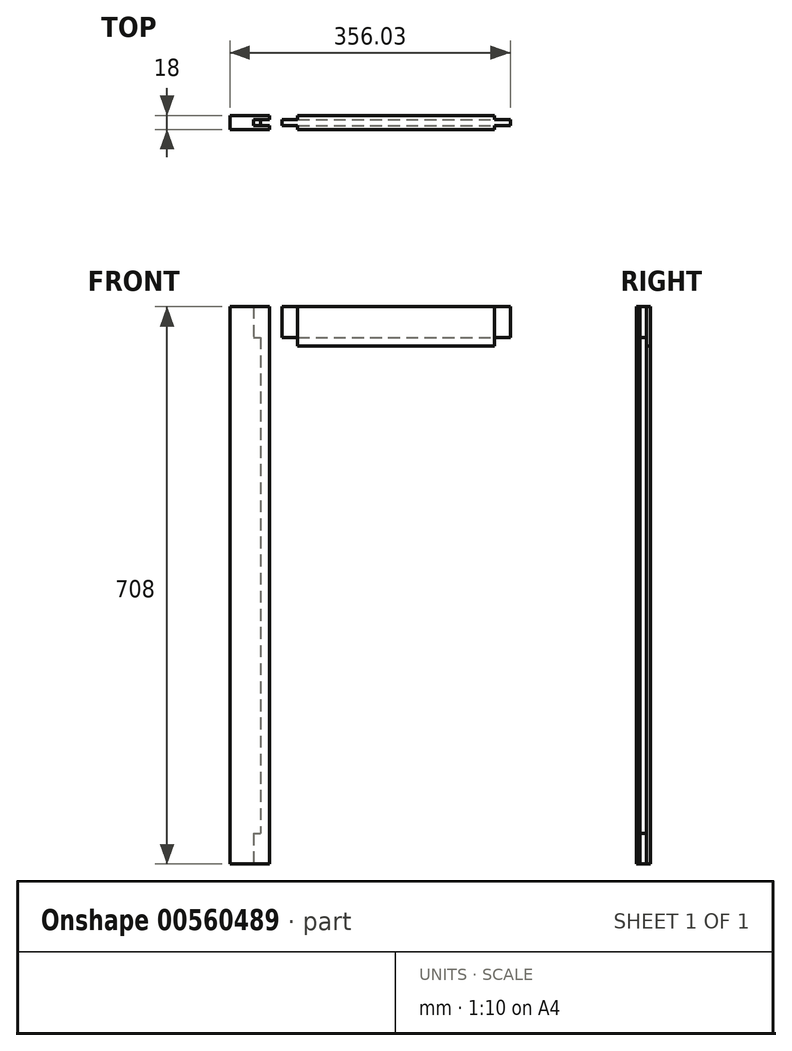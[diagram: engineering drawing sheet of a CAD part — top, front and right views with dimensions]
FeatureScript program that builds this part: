
annotation { "Feature Type Name" : "Feature", "Feature Type Description" : "" }
export const myFeature = defineFeature(function(context is Context, id is Id, definition is map)
    precondition{}
    {
        {
            var Q0;
            Q0=qCreatedBy(makeId("Front.planeOp"),FACE);
            var sketch = newSketch(context, id + "F0", { "sketchPlane" : qUnion([Q0])});
            skLineSegment(sketch, "E0.bottom", {"start": v(-16.71, 354) * mm, "end": v(-66.71, 354) * mm});
            skLineSegment(sketch, "E0.top", {"start": v(-16.71, -354) * mm, "end": v(-66.71, -354) * mm});
            skLineSegment(sketch, "E0.left", {"start": v(-16.71, 354) * mm, "end": v(-16.71, -354) * mm});
            skLineSegment(sketch, "E0.right", {"start": v(-66.71, 354) * mm, "end": v(-66.71, -354) * mm});
            skPoint(sketch, "E0.middle", {"position": v(-41.71, 0) * mm});
            skLineSegment(sketch, "E1.bottom", {"start": v(344.89, 354) * mm, "end": v(294.89, 354) * mm});
            skLineSegment(sketch, "E1.top", {"start": v(344.89, -354) * mm, "end": v(294.89, -354) * mm});
            skLineSegment(sketch, "E1.left", {"start": v(344.89, 354) * mm, "end": v(344.89, -354) * mm});
            skLineSegment(sketch, "E1.right", {"start": v(294.89, 354) * mm, "end": v(294.89, -354) * mm});
            skPoint(sketch, "E1.middle", {"position": v(319.89, 0) * mm});
            skLineSegment(sketch, "E2.bottom", {"start": v(19.32, 354) * mm, "end": v(269.32, 354) * mm});
            skLineSegment(sketch, "E2.top", {"start": v(19.32, 304) * mm, "end": v(269.32, 304) * mm});
            skLineSegment(sketch, "E2.left", {"start": v(19.32, 354) * mm, "end": v(19.32, 304) * mm});
            skLineSegment(sketch, "E2.right", {"start": v(269.32, 354) * mm, "end": v(269.32, 304) * mm});
            skLineSegment(sketch, "E3.bottom", {"start": v(19.32, -354) * mm, "end": v(269.32, -354) * mm});
            skLineSegment(sketch, "E3.top", {"start": v(19.32, -304) * mm, "end": v(269.32, -304) * mm});
            skLineSegment(sketch, "E3.left", {"start": v(19.32, -354) * mm, "end": v(19.32, -304) * mm});
            skLineSegment(sketch, "E3.right", {"start": v(269.32, -354) * mm, "end": v(269.32, -304) * mm});
            skSolve(sketch);
        }
        {
            var Q0;
            Q0=makeQuery(id+"F0.imprint","IMPRINT",FACE,{"disambiguationData":[TD([[makeQuery(id+"F0.imprint","IMPRINT",EDGE,{"derivedFrom":sQuery(id+"F0.wireOp",EDGE,"E2.bottom")}),-1.0]])]});
            var Q1;
            Q1=makeQuery(id+"F0.imprint","IMPRINT",FACE,{"disambiguationData":[TD([[makeQuery(id+"F0.imprint","IMPRINT",EDGE,{"derivedFrom":sQuery(id+"F0.wireOp",EDGE,"E0.bottom")}),1.0]])]});
            var Q2;
            Q2=makeQuery(id+"F0.imprint","IMPRINT",FACE,{"disambiguationData":[TD([[makeQuery(id+"F0.imprint","IMPRINT",EDGE,{"derivedFrom":sQuery(id+"F0.wireOp",EDGE,"E1.bottom")}),1.0]])]});
            var Q3;
            Q3=makeQuery(id+"F0.imprint","IMPRINT",FACE,{"disambiguationData":[TD([[makeQuery(id+"F0.imprint","IMPRINT",EDGE,{"derivedFrom":sQuery(id+"F0.wireOp",EDGE,"E3.bottom")}),1.0]])]});
            extrude(context, id + "F1", {"entities" : qUnion([Q0, Q1, Q2, Q3]), "endBound" : BoundingType.SYMMETRIC, "depth" : 18 * mm, "offsetDistance" : 25 * mm});
        }
        {
            var Q0;
            Q0=makeQuery(id+"F1.opExtrude","SWEPT_FACE",FACE,{"disambiguationData":[OSD([sQuery(id+"F0.wireOp",EDGE,"E0.left")])]});
            var sketch = newSketch(context, id + "F2", { "sketchPlane" : qUnion([Q0])});
            skLineSegment(sketch, "E4.bottom", {"start": v(-4, 354) * mm, "end": v(4, 354) * mm});
            skLineSegment(sketch, "E4.top", {"start": v(-4, -354) * mm, "end": v(4, -354) * mm});
            skLineSegment(sketch, "E4.left", {"start": v(-4, 354) * mm, "end": v(-4, -354) * mm});
            skLineSegment(sketch, "E4.right", {"start": v(4, 354) * mm, "end": v(4, -354) * mm});
            skPoint(sketch, "E4.middle", {"position": v(0, 0) * mm});
            skSolve(sketch);
        }
        {
            var Q0;
            Q0=makeQuery(id+"F2.imprint","IMPRINT",FACE,{"disambiguationData":[TD([[makeQuery(id+"F2.imprint","IMPRINT",EDGE,{"derivedFrom":sQuery(id+"F2.wireOp",EDGE,"E4.bottom")}),-1.0]])]});
            extrude(context, id + "F3", {"entities" : qUnion([Q0]), "operationType" : NewBodyOperationType.REMOVE, "oppositeDirection" : true, "depth" : 11 * mm, "offsetDistance" : 25 * mm});
        }
        {
            var Q0;
            Q0=makeQuery(id+"F3.boolean.opBoolean","COPY",FACE,{"derivedFrom":makeQuery(id+"F3.opExtrude","CAP_FACE",FACE,{"disambiguationData":[OSD([sQuery(id+"F2.wireOp",EDGE,"E4.bottom"),sQuery(id+"F2.wireOp",EDGE,"E4.top"),sQuery(id+"F2.wireOp",EDGE,"E4.left"),sQuery(id+"F2.wireOp",EDGE,"E4.right")])],"isStart":false})});
            var sketch = newSketch(context, id + "F4", { "sketchPlane" : qUnion([Q0])});
            skLineSegment(sketch, "E5.bottom", {"start": v(-4, 354) * mm, "end": v(4, 354) * mm});
            skLineSegment(sketch, "E5.top", {"start": v(-4, 315) * mm, "end": v(4, 315) * mm});
            skLineSegment(sketch, "E5.left", {"start": v(-4, 354) * mm, "end": v(-4, 315) * mm});
            skLineSegment(sketch, "E5.right", {"start": v(4, 354) * mm, "end": v(4, 315) * mm});
            skLineSegment(sketch, "E6.bottom", {"start": v(4, -354) * mm, "end": v(-4, -354) * mm});
            skLineSegment(sketch, "E6.top", {"start": v(4, -315) * mm, "end": v(-4, -315) * mm});
            skLineSegment(sketch, "E6.left", {"start": v(4, -354) * mm, "end": v(4, -315) * mm});
            skLineSegment(sketch, "E6.right", {"start": v(-4, -354) * mm, "end": v(-4, -315) * mm});
            skSolve(sketch);
        }
        {
            var Q0;
            Q0=makeQuery(id+"F4.imprint","IMPRINT",FACE,{"disambiguationData":[TD([[makeQuery(id+"F4.imprint","IMPRINT",EDGE,{"derivedFrom":sQuery(id+"F4.wireOp",EDGE,"E5.bottom")}),-1.0]])]});
            var Q1;
            Q1=makeQuery(id+"F4.imprint","IMPRINT",FACE,{"disambiguationData":[TD([[makeQuery(id+"F4.imprint","IMPRINT",EDGE,{"derivedFrom":sQuery(id+"F4.wireOp",EDGE,"E6.bottom")}),1.0]])]});
            extrude(context, id + "F5", {"entities" : qUnion([Q0, Q1]), "operationType" : NewBodyOperationType.REMOVE, "oppositeDirection" : true, "depth" : 9 * mm, "offsetDistance" : 25 * mm});
        }
        {
            var Q0;
            Q0=makeQuery(id+"F1.opExtrude","SWEPT_FACE",FACE,{"disambiguationData":[OSD([sQuery(id+"F0.wireOp",EDGE,"E1.right")])]});
            var sketch = newSketch(context, id + "F6", { "sketchPlane" : qUnion([Q0])});
            skLineSegment(sketch, "E7.bottom", {"start": v(4, 354) * mm, "end": v(-4, 354) * mm});
            skLineSegment(sketch, "E7.top", {"start": v(4, -354) * mm, "end": v(-4, -354) * mm});
            skLineSegment(sketch, "E7.left", {"start": v(4, 354) * mm, "end": v(4, -354) * mm});
            skLineSegment(sketch, "E7.right", {"start": v(-4, 354) * mm, "end": v(-4, -354) * mm});
            skPoint(sketch, "E7.middle", {"position": v(0, 0) * mm});
            skSolve(sketch);
        }
        {
            var Q0;
            Q0=makeQuery(id+"F6.imprint","IMPRINT",FACE,{"disambiguationData":[TD([[makeQuery(id+"F6.imprint","IMPRINT",EDGE,{"derivedFrom":sQuery(id+"F6.wireOp",EDGE,"E7.bottom")}),1.0]])]});
            extrude(context, id + "F7", {"entities" : qUnion([Q0]), "operationType" : NewBodyOperationType.REMOVE, "oppositeDirection" : true, "depth" : 11 * mm, "offsetDistance" : 25 * mm});
        }
        {
            var Q0;
            Q0=makeQuery(id+"F7.boolean.opBoolean","COPY",FACE,{"derivedFrom":makeQuery(id+"F7.opExtrude","CAP_FACE",FACE,{"disambiguationData":[OSD([sQuery(id+"F6.wireOp",EDGE,"E7.bottom"),sQuery(id+"F6.wireOp",EDGE,"E7.top"),sQuery(id+"F6.wireOp",EDGE,"E7.left"),sQuery(id+"F6.wireOp",EDGE,"E7.right")])],"isStart":false})});
            var sketch = newSketch(context, id + "F8", { "sketchPlane" : qUnion([Q0])});
            skLineSegment(sketch, "E8.bottom", {"start": v(4, -354) * mm, "end": v(-4, -354) * mm});
            skLineSegment(sketch, "E8.top", {"start": v(4, -304) * mm, "end": v(-4, -304) * mm});
            skLineSegment(sketch, "E8.left", {"start": v(4, -354) * mm, "end": v(4, -304) * mm});
            skLineSegment(sketch, "E8.right", {"start": v(-4, -354) * mm, "end": v(-4, -304) * mm});
            skLineSegment(sketch, "E9.bottom", {"start": v(-4, 354) * mm, "end": v(4, 354) * mm});
            skLineSegment(sketch, "E9.top", {"start": v(-4, 304) * mm, "end": v(4, 304) * mm});
            skLineSegment(sketch, "E9.left", {"start": v(-4, 354) * mm, "end": v(-4, 304) * mm});
            skLineSegment(sketch, "E9.right", {"start": v(4, 354) * mm, "end": v(4, 304) * mm});
            skSolve(sketch);
        }
        {
            var Q0;
            Q0=makeQuery(id+"F8.imprint","IMPRINT",FACE,{"disambiguationData":[TD([[makeQuery(id+"F8.imprint","IMPRINT",EDGE,{"derivedFrom":sQuery(id+"F8.wireOp",EDGE,"E9.bottom")}),1.0]])]});
            var Q1;
            Q1=makeQuery(id+"F8.imprint","IMPRINT",FACE,{"disambiguationData":[TD([[makeQuery(id+"F8.imprint","IMPRINT",EDGE,{"derivedFrom":sQuery(id+"F8.wireOp",EDGE,"E8.bottom")}),-1.0]])]});
            extrude(context, id + "F9", {"entities" : qUnion([Q0, Q1]), "operationType" : NewBodyOperationType.REMOVE, "oppositeDirection" : true, "depth" : 9 * mm, "offsetDistance" : 25 * mm});
        }
        {
            var Q0;
            Q0=makeQuery(id+"F1.opExtrude","SWEPT_FACE",FACE,{"disambiguationData":[OSD([sQuery(id+"F0.wireOp",EDGE,"E2.top")])]});
            var sketch = newSketch(context, id + "F10", { "sketchPlane" : qUnion([Q0])});
            skPoint(sketch, "E10.oppositeSnap0", {"position": v(19.32, 0) * mm});
            skLineSegment(sketch, "E10.bottom", {"start": v(19.32, -4) * mm, "end": v(269.32, -4) * mm});
            skLineSegment(sketch, "E10.top", {"start": v(19.32, 4) * mm, "end": v(269.32, 4) * mm});
            skLineSegment(sketch, "E10.left", {"start": v(19.32, -4) * mm, "end": v(19.32, 4) * mm});
            skLineSegment(sketch, "E10.right", {"start": v(269.32, -4) * mm, "end": v(269.32, 4) * mm});
            skSolve(sketch);
        }
        {
            var Q0;
            Q0=makeQuery(id+"F10.imprint","IMPRINT",FACE,{"disambiguationData":[TD([[makeQuery(id+"F10.imprint","IMPRINT",EDGE,{"derivedFrom":sQuery(id+"F10.wireOp",EDGE,"E10.bottom")}),1.0]])]});
            extrude(context, id + "F11", {"entities" : qUnion([Q0]), "operationType" : NewBodyOperationType.REMOVE, "oppositeDirection" : true, "depth" : 11 * mm, "offsetDistance" : 25 * mm});
        }
        {
            var Q0;
            Q0=makeQuery(id+"F1.opExtrude","SWEPT_FACE",FACE,{"disambiguationData":[OSD([sQuery(id+"F0.wireOp",EDGE,"E2.left")])]});
            var sketch = newSketch(context, id + "F12", { "sketchPlane" : qUnion([Q0])});
            skLineSegment(sketch, "E11.bottom", {"start": v(-4, 315) * mm, "end": v(4, 315) * mm});
            skLineSegment(sketch, "E11.top", {"start": v(-4, 354) * mm, "end": v(4, 354) * mm});
            skLineSegment(sketch, "E11.left", {"start": v(-4, 315) * mm, "end": v(-4, 354) * mm});
            skLineSegment(sketch, "E11.right", {"start": v(4, 315) * mm, "end": v(4, 354) * mm});
            skSolve(sketch);
        }
        {
            var Q0;
            Q0=makeQuery(id+"F12.imprint","IMPRINT",FACE,{"disambiguationData":[TD([[makeQuery(id+"F12.imprint","IMPRINT",EDGE,{"derivedFrom":sQuery(id+"F12.wireOp",EDGE,"E11.bottom")}),-1.0]])]});
            extrude(context, id + "F13", {"entities" : qUnion([Q0]), "operationType" : NewBodyOperationType.ADD, "depth" : 20 * mm, "offsetDistance" : 25 * mm});
        }
        {
            var Q0;
            Q0=makeQuery(id+"F1.opExtrude","SWEPT_FACE",FACE,{"disambiguationData":[OSD([sQuery(id+"F0.wireOp",EDGE,"E2.right")])]});
            var sketch = newSketch(context, id + "F14", { "sketchPlane" : qUnion([Q0])});
            skLineSegment(sketch, "E12.bottom", {"start": v(-4, 315) * mm, "end": v(4, 315) * mm});
            skLineSegment(sketch, "E12.top", {"start": v(-4, 354) * mm, "end": v(4, 354) * mm});
            skLineSegment(sketch, "E12.left", {"start": v(-4, 315) * mm, "end": v(-4, 354) * mm});
            skLineSegment(sketch, "E12.right", {"start": v(4, 315) * mm, "end": v(4, 354) * mm});
            skSolve(sketch);
        }
        {
            var Q0;
            Q0=makeQuery(id+"F14.imprint","IMPRINT",FACE,{"disambiguationData":[TD([[makeQuery(id+"F14.imprint","IMPRINT",EDGE,{"derivedFrom":sQuery(id+"F14.wireOp",EDGE,"E12.bottom")}),1.0]])]});
            extrude(context, id + "F15", {"entities" : qUnion([Q0]), "operationType" : NewBodyOperationType.ADD, "depth" : 20 * mm, "offsetDistance" : 25 * mm});
        }
        {
            var Q0;
            Q0=makeQuery(id+"F1.opExtrude","SWEPT_BODY",BODY,{"disambiguationData":[OSD([sQuery(id+"F0.wireOp",EDGE,"E1.bottom"),sQuery(id+"F0.wireOp",EDGE,"E1.top"),sQuery(id+"F0.wireOp",EDGE,"E1.left"),sQuery(id+"F0.wireOp",EDGE,"E1.right")])]});
            deleteBodies(context, id + "F16", {"entities" : qUnion([Q0])});
        }
        {
            var Q0;
            Q0=makeQuery(id+"F1.opExtrude","SWEPT_BODY",BODY,{"disambiguationData":[OSD([sQuery(id+"F0.wireOp",EDGE,"E3.bottom"),sQuery(id+"F0.wireOp",EDGE,"E3.top"),sQuery(id+"F0.wireOp",EDGE,"E3.left"),sQuery(id+"F0.wireOp",EDGE,"E3.right")])]});
            deleteBodies(context, id + "F17", {"entities" : qUnion([Q0])});
        }
    });
